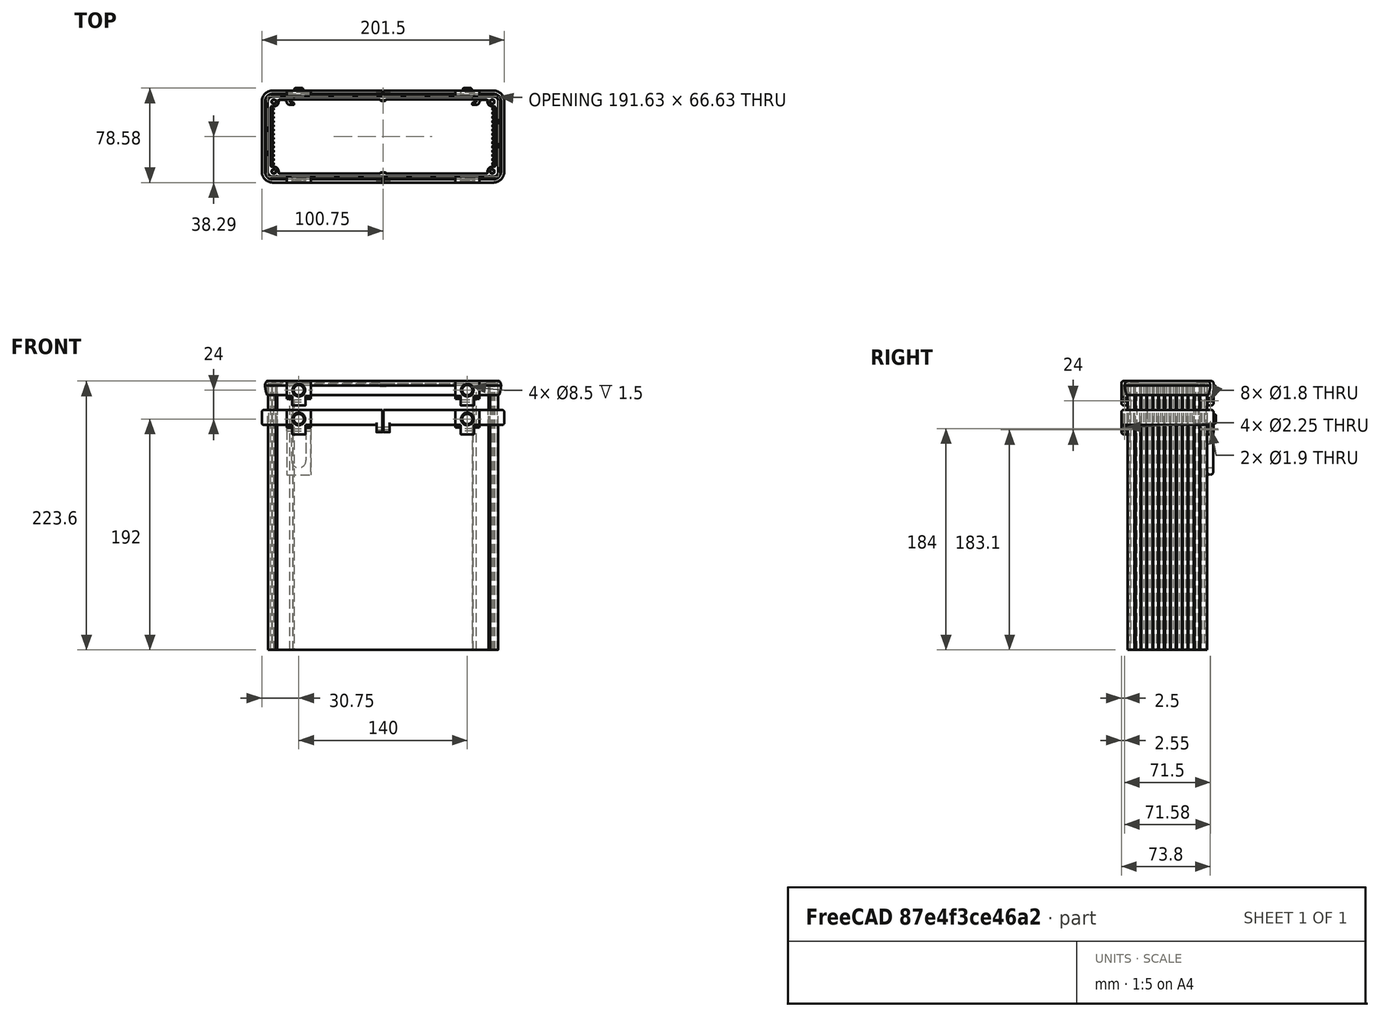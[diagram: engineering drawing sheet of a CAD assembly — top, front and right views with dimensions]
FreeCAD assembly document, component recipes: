
FREECAD ASSEMBLY — COMPONENT RECIPES ("BevelHinge")

This assembly document has 2 components, labeled P0..P1 below (a component is one placed body or linked part). 2 of them carry a construction recipe — the FreeCAD feature program that regenerates the part from scratch, quoted from this document or its linked companion documents; the rest are supplied as boundary geometry only. No exploded tour is included for this assembly.
COMPONENT P0 — recipe-attached ("Body002", modeled in this document).
Construction recipe (the document's own serialized feature program — sketch geometry with constraints, then the solid features built on it; lengths are millimeters unless a unit is written):

FEATURE [Sketcher::SketchObject] Sketch
  ArcFitTolerance = 1e-06
  AttachmentSupport = -> [XZ_Plane]
  FullyConstrained = true
  MakeInternals = false
  MapMode = 5
  Placement = pos=(0,0,0) rot=(1,0,0;1.5708rad)
  sketch-geometry (11):
    g0: LineSegment StartX=-4.5 StartY=-1.2 StartZ=0 EndX=1.812e-13 EndY=-1.2 EndZ=0
    g1: LineSegment StartX=1.812e-13 StartY=-1.2 StartZ=0 EndX=1.812e-13 EndY=3.6 EndZ=0
    g2: LineSegment StartX=-4.5 StartY=-1.2 StartZ=0 EndX=-4.5 EndY=-6.7 EndZ=0
    g3: LineSegment StartX=-4.5 StartY=-6.7 StartZ=0 EndX=-15.5 EndY=-6.7 EndZ=0
    g4: LineSegment StartX=-15.5 StartY=-6.7 StartZ=0 EndX=-15.5 EndY=-1.2 EndZ=0
    g5: LineSegment StartX=-15.5 StartY=-1.2 StartZ=0 EndX=-20 EndY=-1.2 EndZ=0
    g6: LineSegment StartX=-20 StartY=-1.2 StartZ=0 EndX=-20 EndY=3.6 EndZ=0
    g7: ArcOfCircle [constr] CenterX=-10 CenterY=3.6 CenterZ=0 NormalX=0 NormalY=0 NormalZ=1 AngleXU=0 Radius=10 StartAngle=-2.64579e-11 EndAngle=3.14159
    g8: LineSegment StartX=-20 StartY=3.6 StartZ=0 EndX=-20 EndY=13.6 EndZ=0
    g9: LineSegment StartX=-20 StartY=13.6 StartZ=0 EndX=1.812e-13 EndY=13.6 EndZ=0
    g10: LineSegment StartX=1.812e-13 StartY=3.6 StartZ=0 EndX=1.812e-13 EndY=13.6 EndZ=0
  constraints (31):
    c: Horizontal(g0)
    c: Coincident(g0,g1)
    c: Vertical(g1)
    c: Coincident(g0,g2)
    c: Vertical(g2)
    c: Coincident(g2,g3)
    c: Horizontal(g3)
    c: Coincident(g3,g4)
    c: Vertical(g4)
    c: Coincident(g4,g5)
    c: Horizontal(g5)
    c: Coincident(g5,g6)
    c: Vertical(g6)
    c: Tangent(g7,g6) = 1.5708
    c: Tangent(g7,g1) = -1.5708
    c: DistanceX(g3,g3) = 11
    c: DistanceY(g4,g4) = 5.5
    c: Equal(g0,g5)
    c: DistanceX(g5,g5) = 4.5
    c: PointOnObject(g0,g-2)
    c: DistanceY(g0,g-1) = 1.2
    c: DistanceY(g6,g6) = 4.8
    c: Equal(g6,g1)
    c: Coincident(g8,g6)
    c: Vertical(g8)
    c: Horizontal(g9)
    c: Coincident(g10,g9)
    c: Vertical(g10)
    c: Coincident(g10,g1)
    c: Coincident(g8,g9)
    c: Tangent(g7,g9)
FEATURE [PartDesign::Pad] Pad
  Direction = (0,-1,2e-16)
  Length = 5
  Length2 = 10
  Placement = pos=(0,0,0) rot=(1,0,0;1.5708rad)
  Profile = -> Sketch
  ReferenceAxis = -> Sketch [N_Axis]
  Suppressed = false
  Type = 0
FEATURE [Sketcher::SketchObject] Sketch001
  ArcFitTolerance = 1e-06
  AttachmentSupport = -> [Pad]
  ExternalGeometry = -> [Pad]
  FullyConstrained = true
  MakeInternals = false
  MapMode = 5
  Placement = pos=(1.812e-13,0,0) rot=(0.707107,0,0.707107;3.14159rad)
  sketch-geometry (3):
    g0: LineSegment StartX=-1.2 StartY=0 StartZ=0 EndX=1 EndY=5 EndZ=0
    g1: LineSegment StartX=1 StartY=5 StartZ=0 EndX=-1.2 EndY=5 EndZ=0
    g2: LineSegment StartX=-1.2 StartY=5 StartZ=0 EndX=-1.2 EndY=0 EndZ=0
  constraints (8):
    c: Coincident(g0,g1)
    c: Horizontal(g1)
    c: Coincident(g1,g2)
    c: Vertical(g2)
    c: Coincident(g0,g2)
    c: Coincident(g0,g-3)
    c: PointOnObject(g0,g-4)
    c: DistanceX(g-1,g0) = 1
FEATURE [PartDesign::Pocket] Pocket
  BaseFeature = -> Pad
  Direction = (-1,0,2e-16)
  Length = 0
  Length2 = 5
  Placement = pos=(0,0,0) rot=(1,0,0;1.5708rad)
  Profile = -> Sketch001
  ReferenceAxis = -> Sketch001 [N_Axis]
  Suppressed = false
  Type = 3
  UpToFace = -> Pad [Face10]
FEATURE [PartDesign::SubShapeBinder] Binder
  BindCopyOnChange = 0
  BindMode = 0
  ClaimChildren = false
  Context = -> Body [Binder.]
  Fuse = false
  MakeFace = true
  OffsetFill = false
  OffsetIntersection = false
  OffsetJoinType = 0
  OffsetOpenResult = false
  PartialLoad = false
  Placement = pos=(-22,0,0) rot=(0,0,1;0rad)
  Relative = true
  Support = -> [Sketch001]
  _Version = 2
FEATURE [PartDesign::Pocket] Pocket001
  BaseFeature = -> Pocket
  Direction = (-1,0,2e-16)
  Length = 0
  Length2 = 5
  Placement = pos=(0,0,0) rot=(1,0,0;1.5708rad)
  Profile = -> Binder
  Reversed = true
  Suppressed = false
  Type = 3
  UpToFace = -> Pocket [Face7]
FEATURE [Sketcher::SketchObject] Sketch002
  ArcFitTolerance = 1e-06
  AttachmentSupport = -> [YZ_Plane]
  FullyConstrained = true
  MakeInternals = false
  MapMode = 5
  Placement = pos=(0,0,0) rot=(0.57735,0.57735,0.57735;2.0944rad)
  sketch-geometry (1):
    g0: Circle CenterX=-2.5 CenterY=-2.9 CenterZ=0 NormalX=0 NormalY=0 NormalZ=1 AngleXU=0 Radius=0.9
  constraints (3):
    c: DistanceX(g0) = -2.5
    c: DistanceY(g0) = -2.9
    c: Diameter(g0) = 1.8
FEATURE [PartDesign::Pocket] Pocket002
  BaseFeature = -> Pocket001
  Direction = (-1,0,0)
  Length = 5
  Length2 = 5
  Placement = pos=(0,0,0) rot=(1,0,0;1.5708rad)
  Profile = -> Sketch002
  ReferenceAxis = -> Sketch002 [N_Axis]
  Suppressed = false
  Type = 1
FEATURE [PartDesign::Fillet] Fillet
  Base = -> Pocket002 [Edge26,Edge20]
  BaseFeature = -> Pocket002
  Placement = pos=(0,0,0) rot=(1,0,0;1.5708rad)
  Radius = 2
  SupportTransform = false
  Suppressed = false
  UseAllEdges = false
FEATURE [Sketcher::SketchObject] Sketch005
  ArcFitTolerance = 1e-06
  AttachmentOffset = pos=(0,0,2.5) rot=(0,0,1;0rad)
  AttachmentSupport = -> [XZ_Plane]
  FullyConstrained = true
  MakeInternals = false
  MapMode = 5
  Placement = pos=(0,-2.5,6e-16) rot=(1,0,0;1.5708rad)
  sketch-geometry (1):
    g0: Circle CenterX=-10 CenterY=6 CenterZ=0 NormalX=0 NormalY=0 NormalZ=1 AngleXU=0 Radius=4.25
  constraints (3):
    c: DistanceX(g0,g-1) = 10
    c: DistanceY(g0,g-1) = -6
    c: Diameter(g0) = 8.5
FEATURE [PartDesign::Pocket] Pocket004
  BaseFeature = -> Fillet
  Direction = (0,1,-2e-16)
  Length = 5
  Length2 = 5
  Placement = pos=(0,0,0) rot=(1,0,0;1.5708rad)
  Profile = -> Sketch005
  ReferenceAxis = -> Sketch005 [N_Axis]
  Reversed = true
  Suppressed = false
  Type = 0
FEATURE [PartDesign::Chamfer] Chamfer
  Angle = 45
  Base = -> Pocket004 [Edge18]
  BaseFeature = -> Pocket004
  ChamferType = 0
  FlipDirection = false
  Placement = pos=(0,0,0) rot=(1,0,0;1.5708rad)
  Size = 1
  Size2 = 1
  SupportTransform = false
  Suppressed = false
  UseAllEdges = false
FEATURE [PartDesign::Body] Body
  AllowCompound = false
  Group = -> [Sketch,Pad,Sketch001,Pocket,Binder,Pocket001,Sketch002,Pocket002,Fillet,Sketch005,Pocket004,Chamfer]
  Origin = -> Origin
  Placement = pos=(-60,-66.3,100) rot=(0,0,1;0rad)
  Tip = -> Chamfer
COMPONENT P1 — recipe-attached ("Body003", modeled in this document).
Construction recipe (the document's own serialized feature program — sketch geometry with constraints, then the solid features built on it; lengths are millimeters unless a unit is written):

FEATURE [Sketcher::SketchObject] Sketch003
  ArcFitTolerance = 1e-06
  AttachmentSupport = -> [XZ_Plane001]
  FullyConstrained = true
  MakeInternals = false
  MapMode = 5
  Placement = pos=(0,0,0) rot=(1,0,0;1.5708rad)
  sketch-geometry (8):
    g0: LineSegment StartX=0 StartY=-0.5 StartZ=0 EndX=-4 EndY=-0.5 EndZ=0
    g1: LineSegment StartX=-4 StartY=-0.5 StartZ=0 EndX=-4 EndY=-28.5 EndZ=0
    g2: LineSegment StartX=-16 StartY=-28.5 StartZ=0 EndX=-16 EndY=-0.5 EndZ=0
    g3: LineSegment StartX=-16 StartY=-0.5 StartZ=0 EndX=-20 EndY=-0.5 EndZ=0
    g4: LineSegment StartX=-20 StartY=-0.5 StartZ=0 EndX=-20 EndY=-40.5 EndZ=0
    g5: LineSegment StartX=-20 StartY=-40.5 StartZ=0 EndX=0 EndY=-40.5 EndZ=0
    g6: LineSegment StartX=0 StartY=-40.5 StartZ=0 EndX=0 EndY=-0.5 EndZ=0
    g7: ArcOfCircle CenterX=-10 CenterY=-28.5 CenterZ=0 NormalX=0 NormalY=0 NormalZ=1 AngleXU=0 Radius=6 StartAngle=3.14159 EndAngle=6.28319
  constraints (23):
    c: Horizontal(g0)
    c: Coincident(g0,g1)
    c: Vertical(g1)
    c: Vertical(g2)
    c: Coincident(g2,g3)
    c: Horizontal(g3)
    c: Coincident(g3,g4)
    c: Vertical(g4)
    c: Coincident(g4,g5)
    c: PointOnObject(g5,g-2)
    c: Horizontal(g5)
    c: Coincident(g5,g6)
    c: Coincident(g6,g0)
    c: Vertical(g6)
    c: Tangent(g7,g1) = 1.5708
    c: Tangent(g7,g2) = 1.5708
    c: DistanceX(g3,g3) = 4
    c: Equal(g3,g0)
    c: Equal(g1,g2)
    c: DistanceY(g4,g4) = 40
    c: DistanceY(g2,g2) = 28
    c: DistanceX(g2,g0) = 12
    c: DistanceY(g0,g-1) = 0.5
FEATURE [PartDesign::Pad] Pad001
  Direction = (0,-1,2e-16)
  Length = 5
  Length2 = 10
  Placement = pos=(0,0,0) rot=(1,0,0;1.5708rad)
  Profile = -> Sketch003
  ReferenceAxis = -> Sketch003 [N_Axis]
  Suppressed = false
  Type = 0
FEATURE [Sketcher::SketchObject] Sketch004
  ArcFitTolerance = 1e-06
  AttachmentSupport = -> [YZ_Plane001]
  ExternalGeometry = -> [Pad001]
  FullyConstrained = true
  MakeInternals = false
  MapMode = 5
  Placement = pos=(0,0,0) rot=(0.57735,0.57735,0.57735;2.0944rad)
  sketch-geometry (11):
    g0: Circle CenterX=-2.5 CenterY=-2.9 CenterZ=0 NormalX=0 NormalY=0 NormalZ=1 AngleXU=0 Radius=0.95
    g1: ArcOfCircle CenterX=-2.5 CenterY=-37.8 CenterZ=0 NormalX=0 NormalY=0 NormalZ=1 AngleXU=0 Radius=2.5 StartAngle=3.14159 EndAngle=6.28319
    g2: LineSegment StartX=-5 StartY=-37.8 StartZ=0 EndX=-5 EndY=-2.4 EndZ=0
    g3: LineSegment StartX=-5 StartY=-2.4 StartZ=0 EndX=-3.1 EndY=-0.5 EndZ=0
    g4: ArcOfCircle CenterX=-3.09998 CenterY=-3.59998 CenterZ=0 NormalX=0 NormalY=0 NormalZ=1 AngleXU=0 Radius=3.09998 StartAngle=1e-16 EndAngle=1.5708
    g5: LineSegment StartX=-4e-16 StartY=-3.59998 StartZ=0 EndX=-4e-16 EndY=-37.8 EndZ=0
    g6: LineSegment [constr] StartX=-2.5 StartY=-37.8 StartZ=0 EndX=-2.5 EndY=-40.3 EndZ=0
    g7: LineSegment StartX=-10 StartY=5 StartZ=0 EndX=-10 EndY=-45 EndZ=0
    g8: LineSegment StartX=-10 StartY=-45 StartZ=0 EndX=10 EndY=-45 EndZ=0
    g9: LineSegment StartX=10 StartY=-45 StartZ=0 EndX=10 EndY=5 EndZ=0
    g10: LineSegment StartX=10 StartY=5 StartZ=0 EndX=-10 EndY=5 EndZ=0
  constraints (31):
    c: DistanceX(g0) = -2.5
    c: DistanceY(g0) = -2.9
    c: Diameter(g0) = 1.9
    c: Vertical(g2)
    c: Tangent(g2,g1) = 1.5708
    c: Coincident(g3,g4)
    c: Coincident(g3,g2)
    c: Vertical(g5)
    c: Tangent(g1,g5) = 1.5708
    c: Tangent(g5,g4) = 1.5708
    c: PointOnObject(g4,g-2)
    c: DistanceX(g2,g-1) = 5
    c: PointOnObject(g3,g-3)
    c: DistanceX(g2,g3) = 1.9
    c: Tangent(g4,g-3)
    c: Coincident(g6,g1)
    c: PointOnObject(g6,g1)
    c: Vertical(g6)
    c: DistanceY(g6) = -40.3
    c: DistanceY(g2) = -2.4
    c: Coincident(g7,g8)
    c: Coincident(g8,g9)
    c: Coincident(g9,g10)
    c: Coincident(g10,g7)
    c: Vertical(g7)
    c: Vertical(g9)
    c: Horizontal(g8)
    c: Symmetric(g7,g9,g-2)
    c: DistanceY(g7,g7) = 50
    c: DistanceX(g10,g10) = 20
    c: DistanceY(g9) = 5
FEATURE [PartDesign::Pocket] Pocket003
  BaseFeature = -> Pad001
  Direction = (-1,0,0)
  Length = 5
  Length2 = 5
  Placement = pos=(0,0,0) rot=(1,0,0;1.5708rad)
  Profile = -> Sketch004
  ReferenceAxis = -> Sketch004 [N_Axis]
  Suppressed = false
  Type = 1
FEATURE [PartDesign::Body] Body001  label="Hinge"
  AllowCompound = false
  Group = -> [Sketch003,Pad001,Sketch004,Pocket003]
  Origin = -> Origin001
  Placement = pos=(-60,5,76) rot=(0,0,1;0rad)
  Tip = -> Pocket003
PROVENANCE & LICENSES
A FreeCAD (.FCStd) document from a public repository crawl; recipes are the document's own serialized feature recipes (and, for linked parts, companion documents' recipes).
License: as declared in the source repository (recorded in the dataset sidecar).
